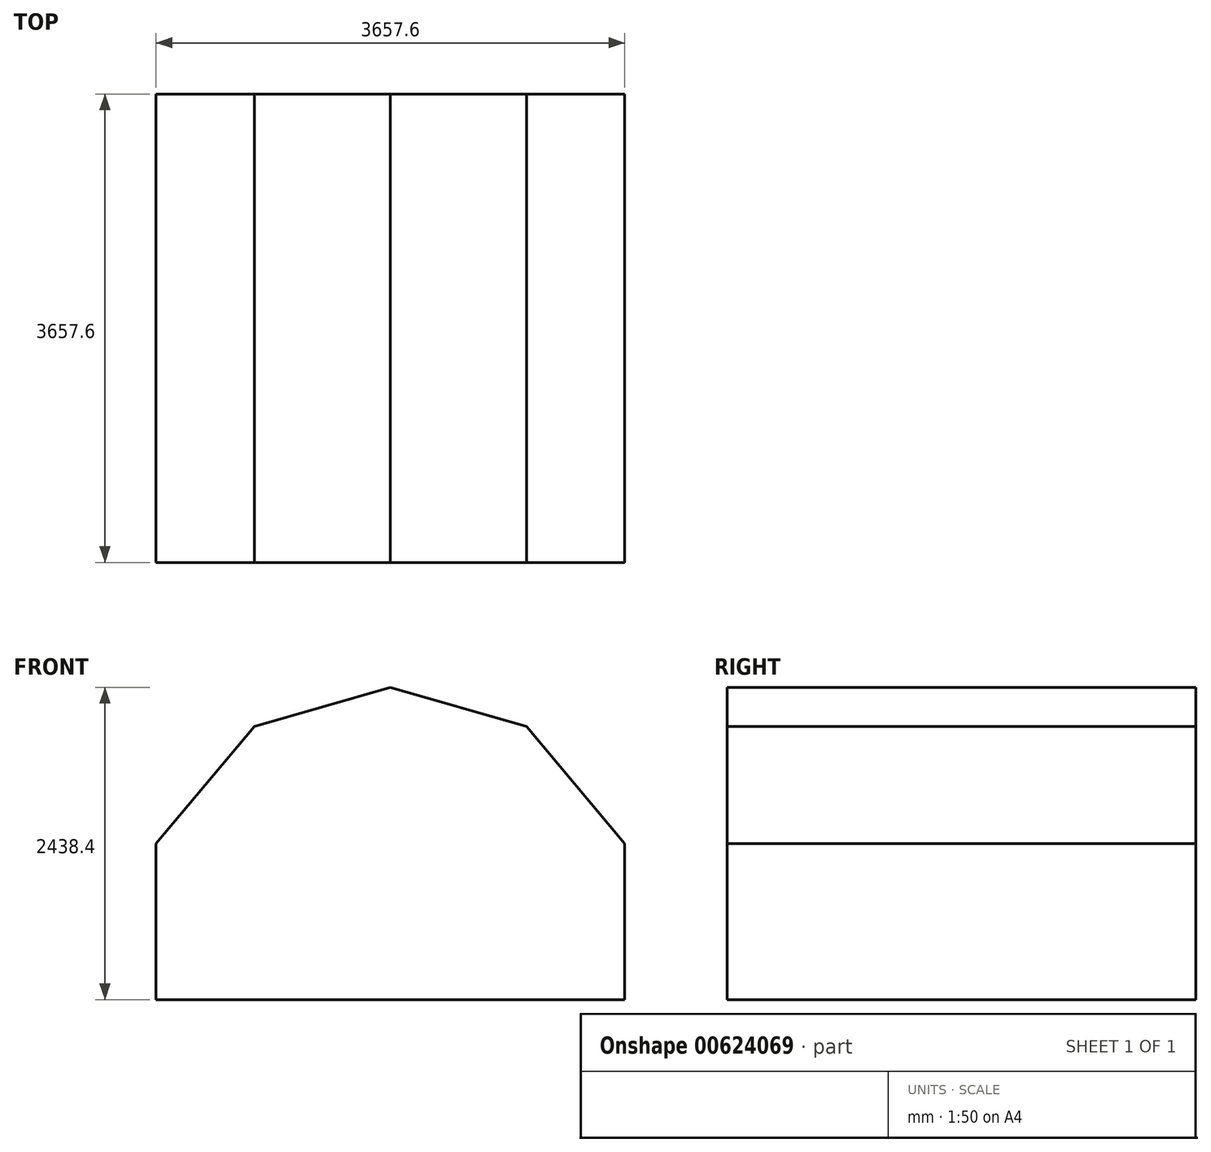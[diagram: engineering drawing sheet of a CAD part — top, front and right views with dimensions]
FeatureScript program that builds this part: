
annotation { "Feature Type Name" : "Feature", "Feature Type Description" : "" }
export const myFeature = defineFeature(function(context is Context, id is Id, definition is map)
    precondition{}
    {
        {
            var Q0;
            Q0=qCreatedBy(makeId("Front.planeOp"),FACE);
            var sketch = newSketch(context, id + "F0", { "sketchPlane" : qUnion([Q0])});
            skLineSegment(sketch, "E0.bottom", {"start": v(1828.8, 1219.2) * mm, "end": v(-1828.8, 1219.2) * mm});
            skLineSegment(sketch, "E0.top", {"start": v(1828.8, -1219.2) * mm, "end": v(-1828.8, -1219.2) * mm});
            skLineSegment(sketch, "E0.left", {"start": v(1828.8, 1219.2) * mm, "end": v(1828.8, -1219.2) * mm});
            skLineSegment(sketch, "E0.right", {"start": v(-1828.8, 1219.2) * mm, "end": v(-1828.8, -1219.2) * mm});
            skPoint(sketch, "E0.middle", {"position": v(0, 0) * mm});
            skSolve(sketch);
        }
        {
            var Q0;
            Q0=makeQuery(id+"F0.imprint","IMPRINT",FACE,{"disambiguationData":[TD([[makeQuery(id+"F0.imprint","IMPRINT",EDGE,{"derivedFrom":sQuery(id+"F0.wireOp",EDGE,"E0.bottom")}),1.0]])]});
            extrude(context, id + "F1", {"entities" : qUnion([Q0]), "oppositeDirection" : true, "depth" : 3657.6 * mm, "offsetDistance" : 25.4 * mm});
        }
        {
            var Q0;
            Q0=makeQuery(id+"F1.opExtrude","CAP_FACE",FACE,{"disambiguationData":[OSD([sQuery(id+"F0.wireOp",EDGE,"E0.bottom"),sQuery(id+"F0.wireOp",EDGE,"E0.top"),sQuery(id+"F0.wireOp",EDGE,"E0.left"),sQuery(id+"F0.wireOp",EDGE,"E0.right")])],"isStart":true});
            var sketch = newSketch(context, id + "F2", { "sketchPlane" : qUnion([Q0])});
            skLineSegment(sketch, "E1", {"start": v(-1828.8, -1219.2) * mm, "end": v(-1828.8, 0) * mm});
            skLineSegment(sketch, "E2", {"start": v(-1828.8, 0) * mm, "end": v(-1061.53, 914.4) * mm});
            skLineSegment(sketch, "E3", {"start": v(-1061.53, 914.4) * mm, "end": v(0, 1219.2) * mm});
            skLineSegment(sketch, "E4", {"start": v(1828.8, 0) * mm, "end": v(1828.8, -1219.2) * mm});
            skLineSegment(sketch, "E5", {"start": v(0, 1219.2) * mm, "end": v(0, -1219.2) * mm});
            skLineSegment(sketch, "E6.MirrorCS", {"start": v(1828.8, 0) * mm, "end": v(1061.53, 914.4) * mm});
            skLineSegment(sketch, "E7.MirrorCS", {"start": v(1061.53, 914.4) * mm, "end": v(0, 1219.2) * mm});
            skPoint(sketch, "E8.start.orphan", {"position": v(-1828.8, 914.4) * mm});
            skPoint(sketch, "E9.start.orphan", {"position": v(-1828.8, 1219.2) * mm});
            skPoint(sketch, "E10.MirrorCS.end.orphan", {"position": v(0, 1219.2) * mm});
            skPoint(sketch, "E10.MirrorCS.start.orphan", {"position": v(1828.8, 1219.2) * mm});
            skLineSegment(sketch, "E11", {"start": v(0, 1219.2) * mm, "end": v(-1828.8, 1219.2) * mm});
            skLineSegment(sketch, "E12", {"start": v(-1828.8, 0) * mm, "end": v(-1828.8, 1219.2) * mm});
            skLineSegment(sketch, "E13", {"start": v(1828.8, 1219.2) * mm, "end": v(1828.8, 0) * mm});
            skLineSegment(sketch, "E14", {"start": v(0, 1219.2) * mm, "end": v(1828.8, 1219.2) * mm});
            skSolve(sketch);
        }
        {
            var Q0;
            Q0=makeQuery(id+"F2.imprint","IMPRINT",FACE,{"disambiguationData":[TD([[makeQuery(id+"F2.imprint","IMPRINT",EDGE,{"derivedFrom":sQuery(id+"F2.wireOp",EDGE,"E2")}),1.0]])]});
            var Q1;
            Q1=makeQuery(id+"F2.imprint","IMPRINT",FACE,{"disambiguationData":[TD([[makeQuery(id+"F2.imprint","IMPRINT",EDGE,{"derivedFrom":sQuery(id+"F2.wireOp",EDGE,"E6.MirrorCS")}),-1.0]])]});
            extrude(context, id + "F3", {"entities" : qUnion([Q0, Q1]), "operationType" : NewBodyOperationType.REMOVE, "oppositeDirection" : true, "depth" : 3657.6 * mm, "offsetDistance" : 25.4 * mm});
        }
    });
